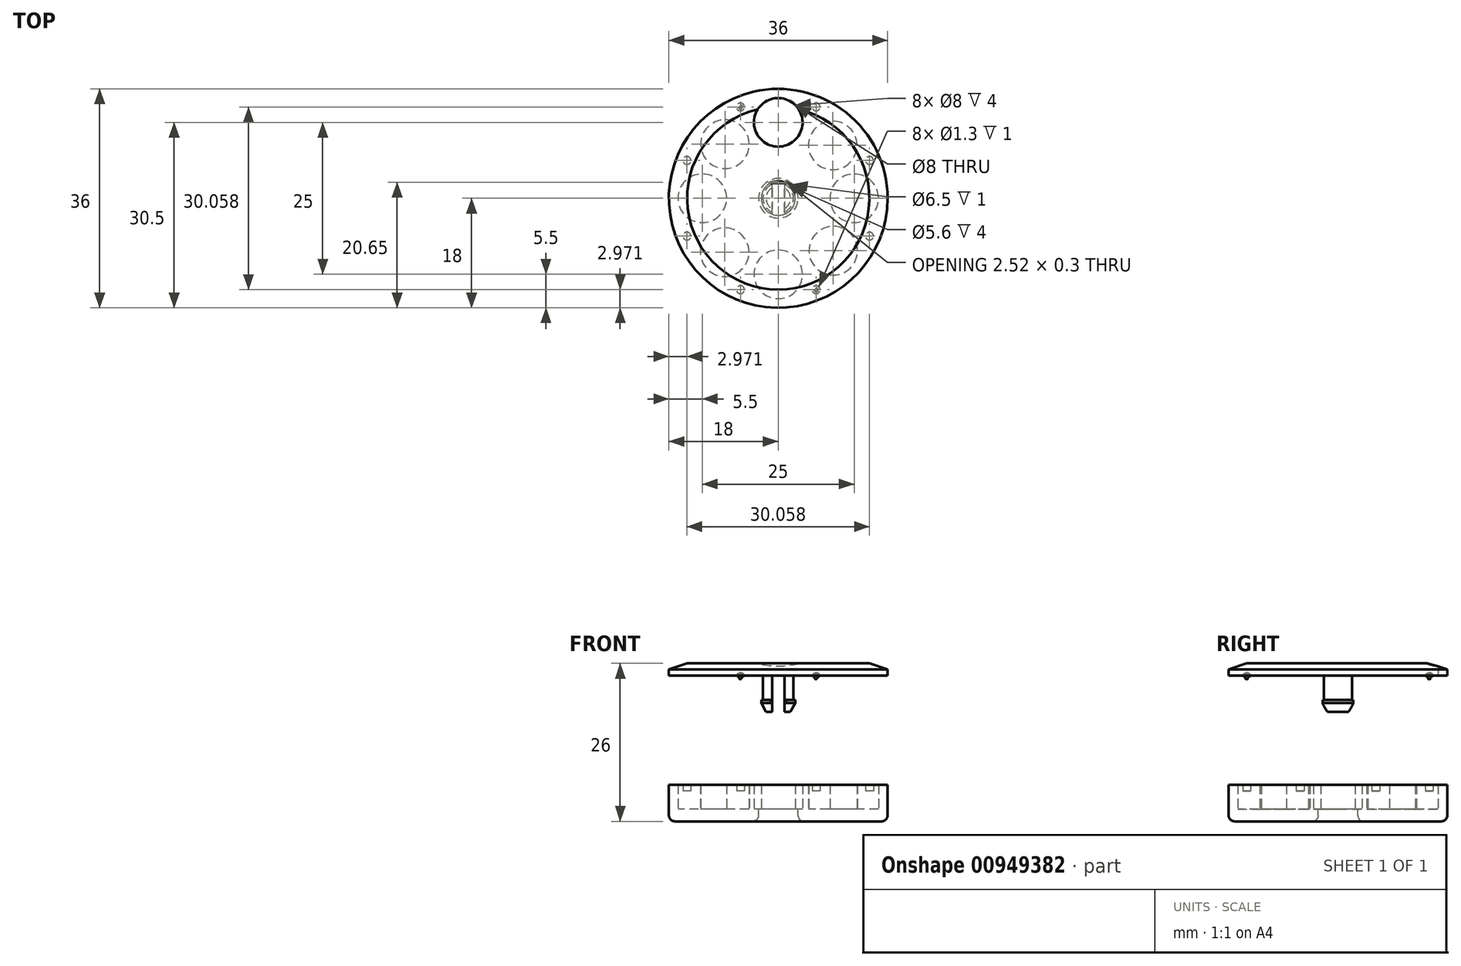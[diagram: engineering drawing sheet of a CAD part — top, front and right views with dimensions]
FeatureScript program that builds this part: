
annotation { "Feature Type Name" : "Feature", "Feature Type Description" : "" }
export const myFeature = defineFeature(function(context is Context, id is Id, definition is map)
    precondition{}
    {
        {
            var Q0;
            Q0=qCreatedBy(makeId("Top.planeOp"),FACE);
            var sketch = newSketch(context, id + "F0", { "sketchPlane" : qUnion([Q0])});
            skCircle(sketch, "E0", {"center": v(0, 0) * mm, "radius": 18 * mm});
            skCircle(sketch, "E1", {"center": v(0, 0) * mm, "radius": 12.5 * mm, "construction": true});
            skCircle(sketch, "E2", {"center": v(0, 12.5) * mm, "radius": 4 * mm});
            skCircle(sketch, "E3", {"center": v(12.5, 0) * mm, "radius": 4 * mm});
            skCircle(sketch, "E4", {"center": v(0, -12.5) * mm, "radius": 4 * mm});
            skCircle(sketch, "E5", {"center": v(-12.5, 0) * mm, "radius": 4 * mm});
            skCircle(sketch, "E6", {"center": v(8.97, 8.7) * mm, "radius": 4 * mm});
            skCircle(sketch, "E7", {"center": v(9.05, -8.62) * mm, "radius": 4 * mm});
            skCircle(sketch, "E8", {"center": v(-8.82, -8.86) * mm, "radius": 4 * mm});
            skCircle(sketch, "E9", {"center": v(-8.77, 8.9) * mm, "radius": 4 * mm});
            skCircle(sketch, "E10", {"center": v(0, 0) * mm, "radius": 2.5 * mm});
            skCircle(sketch, "E11", {"center": v(0, 0) * mm, "radius": 3.25 * mm});
            skLineSegment(sketch, "E12.bottom", {"start": v(1, 3.25) * mm, "end": v(-1, 3.25) * mm});
            skLineSegment(sketch, "E12.top", {"start": v(1, -3.25) * mm, "end": v(-1, -3.25) * mm});
            skLineSegment(sketch, "E12.left", {"start": v(1, 3.25) * mm, "end": v(1, -3.25) * mm});
            skLineSegment(sketch, "E12.right", {"start": v(-1, 3.25) * mm, "end": v(-1, -3.25) * mm});
            skLineSegment(sketch, "E13.bottom", {"start": v(3.25, 2.5) * mm, "end": v(-3.25, 2.5) * mm});
            skLineSegment(sketch, "E13.top", {"start": v(3.25, -2.5) * mm, "end": v(-3.25, -2.5) * mm});
            skLineSegment(sketch, "E13.left", {"start": v(3.25, 2.5) * mm, "end": v(3.25, -2.5) * mm});
            skLineSegment(sketch, "E13.right", {"start": v(-3.25, 2.5) * mm, "end": v(-3.25, -2.5) * mm});
            skCircle(sketch, "E14", {"center": v(0, 0) * mm, "radius": 2.8 * mm});
            skSolve(sketch);
        }
        {
            var Q0;
            Q0=makeQuery(id+"F0.imprint","IMPRINT",FACE,{"disambiguationData":[TD([[makeQuery(id+"F0.imprint","IMPRINT",EDGE,{"derivedFrom":sQuery(id+"F0.wireOp",EDGE,"E9")}),1.0]])]});
            var Q1;
            Q1=makeQuery(id+"F0.imprint","IMPRINT",FACE,{"disambiguationData":[TD([[makeQuery(id+"F0.imprint","IMPRINT",EDGE,{"derivedFrom":sQuery(id+"F0.wireOp",EDGE,"E2")}),1.0]])]});
            var Q2;
            Q2=makeQuery(id+"F0.imprint","IMPRINT",FACE,{"disambiguationData":[TD([[makeQuery(id+"F0.imprint","IMPRINT",EDGE,{"derivedFrom":sQuery(id+"F0.wireOp",EDGE,"E3")}),1.0]])]});
            var Q3;
            Q3=makeQuery(id+"F0.imprint","IMPRINT",FACE,{"disambiguationData":[TD([[makeQuery(id+"F0.imprint","IMPRINT",EDGE,{"derivedFrom":sQuery(id+"F0.wireOp",EDGE,"E7")}),1.0]])]});
            var Q4;
            Q4=makeQuery(id+"F0.imprint","IMPRINT",FACE,{"disambiguationData":[TD([[makeQuery(id+"F0.imprint","IMPRINT",EDGE,{"derivedFrom":sQuery(id+"F0.wireOp",EDGE,"E4")}),1.0]])]});
            var Q5;
            Q5=makeQuery(id+"F0.imprint","IMPRINT",FACE,{"disambiguationData":[TD([[makeQuery(id+"F0.imprint","IMPRINT",EDGE,{"derivedFrom":sQuery(id+"F0.wireOp",EDGE,"E6")}),1.0]])]});
            var Q6;
            Q6=makeQuery(id+"F0.imprint","IMPRINT",FACE,{"disambiguationData":[TD([[makeQuery(id+"F0.imprint","IMPRINT",EDGE,{"derivedFrom":sQuery(id+"F0.wireOp",EDGE,"E5")}),1.0]])]});
            var Q7;
            Q7=makeQuery(id+"F0.imprint","IMPRINT",FACE,{"disambiguationData":[TD([[makeQuery(id+"F0.imprint","IMPRINT",EDGE,{"derivedFrom":sQuery(id+"F0.wireOp",EDGE,"E8")}),1.0]])]});
            var Q8;
            Q8=makeQuery(id+"F0.imprint","IMPRINT",FACE,{"disambiguationData":[TD([[makeQuery(id+"F0.imprint","IMPRINT",EDGE,{"derivedFrom":sQuery(id+"F0.wireOp",EDGE,"E2")}),-1.0]])]});
            var Q9;
            {var subQ0=sQuery(id+"F0.wireOp",EDGE,"E12.bottom");var subQ1=sQuery(id+"F0.wireOp",EDGE,"E11");var subQ2=makeQuery(id+"F0.imprint","INTERSECT",VERTEX,{"derivedFrom":[subQ1,subQ0]});Q9=makeQuery(id+"F0.imprint","IMPRINT",FACE,{"disambiguationData":[TD([[makeQuery(id+"F0.imprint","IMPRINT",EDGE,{"disambiguationData":[TD([[subQ2,-1.0]])],"derivedFrom":subQ1}),-1.0]])]});}
            var Q10;
            {var subQ0=sQuery(id+"F0.wireOp",EDGE,"E12.bottom");var subQ1=sQuery(id+"F0.wireOp",EDGE,"E11");var subQ2=makeQuery(id+"F0.imprint","INTERSECT",VERTEX,{"derivedFrom":[subQ1,subQ0]});Q10=makeQuery(id+"F0.imprint","IMPRINT",FACE,{"disambiguationData":[TD([[makeQuery(id+"F0.imprint","IMPRINT",EDGE,{"disambiguationData":[TD([[subQ2,1.0]])],"derivedFrom":subQ1}),-1.0]])]});}
            var Q11;
            {var subQ0=sQuery(id+"F0.wireOp",EDGE,"E12.top");var subQ1=sQuery(id+"F0.wireOp",EDGE,"E11");var subQ2=makeQuery(id+"F0.imprint","INTERSECT",VERTEX,{"derivedFrom":[subQ1,subQ0]});Q11=makeQuery(id+"F0.imprint","IMPRINT",FACE,{"disambiguationData":[TD([[makeQuery(id+"F0.imprint","IMPRINT",EDGE,{"disambiguationData":[TD([[subQ2,-1.0]])],"derivedFrom":subQ1}),-1.0]])]});}
            var Q12;
            {var subQ0=sQuery(id+"F0.wireOp",EDGE,"E12.right");var subQ1=sQuery(id+"F0.wireOp",EDGE,"E11");var subQ2=makeQuery(id+"F0.imprint","INTERSECT",VERTEX,{"disambiguationData":[OD(1.0)],"derivedFrom":[subQ1,subQ0]});Q12=makeQuery(id+"F0.imprint","IMPRINT",FACE,{"disambiguationData":[TD([[makeQuery(id+"F0.imprint","IMPRINT",EDGE,{"disambiguationData":[TD([[subQ2,-1.0]])],"derivedFrom":subQ1}),-1.0]])]});}
            var Q13;
            {var subQ0=sQuery(id+"F0.wireOp",EDGE,"E13.bottom");var subQ1=sQuery(id+"F0.wireOp",EDGE,"E11");var subQ2=makeQuery(id+"F0.imprint","INTERSECT",VERTEX,{"disambiguationData":[OD(0.0)],"derivedFrom":[subQ1,subQ0]});Q13=makeQuery(id+"F0.imprint","IMPRINT",FACE,{"disambiguationData":[TD([[makeQuery(id+"F0.imprint","IMPRINT",EDGE,{"disambiguationData":[TD([[subQ2,1.0]])],"derivedFrom":subQ1}),-1.0]])]});}
            var Q14;
            {var subQ0=sQuery(id+"F0.wireOp",EDGE,"E13.left");var subQ1=sQuery(id+"F0.wireOp",EDGE,"E11");var subQ2=makeQuery(id+"F0.imprint","INTERSECT",VERTEX,{"derivedFrom":[subQ1,subQ0]});Q14=makeQuery(id+"F0.imprint","IMPRINT",FACE,{"disambiguationData":[TD([[makeQuery(id+"F0.imprint","IMPRINT",EDGE,{"disambiguationData":[TD([[subQ2,1.0]])],"derivedFrom":subQ1}),-1.0]])]});}
            var Q15;
            {var subQ0=sQuery(id+"F0.wireOp",EDGE,"E13.right");var subQ1=sQuery(id+"F0.wireOp",EDGE,"E11");var subQ2=makeQuery(id+"F0.imprint","INTERSECT",VERTEX,{"derivedFrom":[subQ1,subQ0]});Q15=makeQuery(id+"F0.imprint","IMPRINT",FACE,{"disambiguationData":[TD([[makeQuery(id+"F0.imprint","IMPRINT",EDGE,{"disambiguationData":[TD([[subQ2,-1.0]])],"derivedFrom":subQ1}),-1.0]])]});}
            var Q16;
            {var subQ0=sQuery(id+"F0.wireOp",EDGE,"E13.bottom");var subQ1=sQuery(id+"F0.wireOp",EDGE,"E11");var subQ2=makeQuery(id+"F0.imprint","INTERSECT",VERTEX,{"disambiguationData":[OD(1.0)],"derivedFrom":[subQ1,subQ0]});Q16=makeQuery(id+"F0.imprint","IMPRINT",FACE,{"disambiguationData":[TD([[makeQuery(id+"F0.imprint","IMPRINT",EDGE,{"disambiguationData":[TD([[subQ2,-1.0]])],"derivedFrom":subQ1}),-1.0]])]});}
            extrude(context, id + "F1", {"entities" : qUnion([Q0, Q1, Q2, Q3, Q4, Q5, Q6, Q7, Q8, Q9, Q10, Q11, Q12, Q13, Q14, Q15, Q16]), "oppositeDirection" : true, "depth" : 2 * mm, "offsetDistance" : 25 * mm});
        }
        {
            var Q0;
            Q0=makeQuery(id+"F0.imprint","IMPRINT",FACE,{"disambiguationData":[TD([[makeQuery(id+"F0.imprint","IMPRINT",EDGE,{"derivedFrom":sQuery(id+"F0.wireOp",EDGE,"E2")}),-1.0]])]});
            var Q1;
            {var subQ0=sQuery(id+"F0.wireOp",EDGE,"E13.bottom");var subQ1=sQuery(id+"F0.wireOp",EDGE,"E11");var subQ2=makeQuery(id+"F0.imprint","INTERSECT",VERTEX,{"disambiguationData":[OD(1.0)],"derivedFrom":[subQ1,subQ0]});Q1=makeQuery(id+"F0.imprint","IMPRINT",FACE,{"disambiguationData":[TD([[makeQuery(id+"F0.imprint","IMPRINT",EDGE,{"disambiguationData":[TD([[subQ2,-1.0]])],"derivedFrom":subQ1}),-1.0]])]});}
            var Q2;
            {var subQ1=sQuery(id+"F0.wireOp",EDGE,"E11");var subQ6=sQuery(id+"F0.wireOp",EDGE,"E12.left");var subQ7=makeQuery(id+"F0.imprint","INTERSECT",VERTEX,{"disambiguationData":[OD(0.0)],"derivedFrom":[subQ1,subQ6]});Q2=makeQuery(id+"F0.imprint","IMPRINT",FACE,{"disambiguationData":[TD([[makeQuery(id+"F0.imprint","IMPRINT",EDGE,{"disambiguationData":[TD([[subQ7,-1.0]])],"derivedFrom":subQ1}),1.0]])]});}
            var Q3;
            {var subQ0=sQuery(id+"F0.wireOp",EDGE,"E12.right");var subQ1=sQuery(id+"F0.wireOp",EDGE,"E11");var subQ2=makeQuery(id+"F0.imprint","INTERSECT",VERTEX,{"disambiguationData":[OD(0.0)],"derivedFrom":[subQ1,subQ0]});Q3=makeQuery(id+"F0.imprint","IMPRINT",FACE,{"disambiguationData":[TD([[makeQuery(id+"F0.imprint","IMPRINT",EDGE,{"disambiguationData":[TD([[subQ2,-1.0]])],"derivedFrom":subQ1}),1.0]])]});}
            var Q4;
            {var subQ0=sQuery(id+"F0.wireOp",EDGE,"E13.bottom");var subQ1=sQuery(id+"F0.wireOp",EDGE,"E11");var subQ2=makeQuery(id+"F0.imprint","INTERSECT",VERTEX,{"disambiguationData":[OD(0.0)],"derivedFrom":[subQ1,subQ0]});Q4=makeQuery(id+"F0.imprint","IMPRINT",FACE,{"disambiguationData":[TD([[makeQuery(id+"F0.imprint","IMPRINT",EDGE,{"disambiguationData":[TD([[subQ2,-1.0]])],"derivedFrom":subQ1}),1.0]])]});}
            var Q5;
            {var subQ1=sQuery(id+"F0.wireOp",EDGE,"E11");var subQ6=sQuery(id+"F0.wireOp",EDGE,"E13.bottom");var subQ7=makeQuery(id+"F0.imprint","INTERSECT",VERTEX,{"disambiguationData":[OD(0.0)],"derivedFrom":[subQ1,subQ6]});Q5=makeQuery(id+"F0.imprint","IMPRINT",FACE,{"disambiguationData":[TD([[makeQuery(id+"F0.imprint","IMPRINT",EDGE,{"disambiguationData":[TD([[subQ7,1.0]])],"derivedFrom":subQ1}),1.0]])]});}
            var Q6;
            {var subQ0=sQuery(id+"F0.wireOp",EDGE,"E12.left");var subQ1=sQuery(id+"F0.wireOp",EDGE,"E11");var subQ2=makeQuery(id+"F0.imprint","INTERSECT",VERTEX,{"disambiguationData":[OD(1.0)],"derivedFrom":[subQ1,subQ0]});Q6=makeQuery(id+"F0.imprint","IMPRINT",FACE,{"disambiguationData":[TD([[makeQuery(id+"F0.imprint","IMPRINT",EDGE,{"disambiguationData":[TD([[subQ2,-1.0]])],"derivedFrom":subQ1}),1.0]])]});}
            var Q7;
            {var subQ0=sQuery(id+"F0.wireOp",EDGE,"E13.left");var subQ1=sQuery(id+"F0.wireOp",EDGE,"E11");var subQ2=makeQuery(id+"F0.imprint","INTERSECT",VERTEX,{"derivedFrom":[subQ1,subQ0]});Q7=makeQuery(id+"F0.imprint","IMPRINT",FACE,{"disambiguationData":[TD([[makeQuery(id+"F0.imprint","IMPRINT",EDGE,{"disambiguationData":[TD([[subQ2,1.0]])],"derivedFrom":subQ1}),-1.0]])]});}
            var Q8;
            {var subQ0=sQuery(id+"F0.wireOp",EDGE,"E13.bottom");var subQ1=sQuery(id+"F0.wireOp",EDGE,"E11");var subQ2=makeQuery(id+"F0.imprint","INTERSECT",VERTEX,{"disambiguationData":[OD(0.0)],"derivedFrom":[subQ1,subQ0]});Q8=makeQuery(id+"F0.imprint","IMPRINT",FACE,{"disambiguationData":[TD([[makeQuery(id+"F0.imprint","IMPRINT",EDGE,{"disambiguationData":[TD([[subQ2,1.0]])],"derivedFrom":subQ1}),-1.0]])]});}
            var Q9;
            {var subQ0=sQuery(id+"F0.wireOp",EDGE,"E13.right");var subQ1=sQuery(id+"F0.wireOp",EDGE,"E11");var subQ2=makeQuery(id+"F0.imprint","INTERSECT",VERTEX,{"derivedFrom":[subQ1,subQ0]});Q9=makeQuery(id+"F0.imprint","IMPRINT",FACE,{"disambiguationData":[TD([[makeQuery(id+"F0.imprint","IMPRINT",EDGE,{"disambiguationData":[TD([[subQ2,-1.0]])],"derivedFrom":subQ1}),-1.0]])]});}
            var Q10;
            {var subQ0=sQuery(id+"F0.wireOp",EDGE,"E12.right");var subQ1=sQuery(id+"F0.wireOp",EDGE,"E11");var subQ2=makeQuery(id+"F0.imprint","INTERSECT",VERTEX,{"disambiguationData":[OD(1.0)],"derivedFrom":[subQ1,subQ0]});Q10=makeQuery(id+"F0.imprint","IMPRINT",FACE,{"disambiguationData":[TD([[makeQuery(id+"F0.imprint","IMPRINT",EDGE,{"disambiguationData":[TD([[subQ2,-1.0]])],"derivedFrom":subQ1}),1.0]])]});}
            var Q11;
            {var subQ0=sQuery(id+"F0.wireOp",EDGE,"E13.top");var subQ1=sQuery(id+"F0.wireOp",EDGE,"E11");var subQ2=makeQuery(id+"F0.imprint","INTERSECT",VERTEX,{"disambiguationData":[OD(0.0)],"derivedFrom":[subQ1,subQ0]});Q11=makeQuery(id+"F0.imprint","IMPRINT",FACE,{"disambiguationData":[TD([[makeQuery(id+"F0.imprint","IMPRINT",EDGE,{"disambiguationData":[TD([[subQ2,-1.0]])],"derivedFrom":subQ1}),1.0]])]});}
            var Q12;
            {var subQ1=sQuery(id+"F0.wireOp",EDGE,"E11");var subQ6=sQuery(id+"F0.wireOp",EDGE,"E13.bottom");var subQ7=makeQuery(id+"F0.imprint","INTERSECT",VERTEX,{"disambiguationData":[OD(1.0)],"derivedFrom":[subQ1,subQ6]});Q12=makeQuery(id+"F0.imprint","IMPRINT",FACE,{"disambiguationData":[TD([[makeQuery(id+"F0.imprint","IMPRINT",EDGE,{"disambiguationData":[TD([[subQ7,-1.0]])],"derivedFrom":subQ1}),1.0]])]});}
            var Q13;
            {var subQ0=sQuery(id+"F0.wireOp",EDGE,"E12.right");var subQ1=sQuery(id+"F0.wireOp",EDGE,"E11");var subQ2=makeQuery(id+"F0.imprint","INTERSECT",VERTEX,{"disambiguationData":[OD(1.0)],"derivedFrom":[subQ1,subQ0]});Q13=makeQuery(id+"F0.imprint","IMPRINT",FACE,{"disambiguationData":[TD([[makeQuery(id+"F0.imprint","IMPRINT",EDGE,{"disambiguationData":[TD([[subQ2,-1.0]])],"derivedFrom":subQ1}),-1.0]])]});}
            var Q14;
            {var subQ0=sQuery(id+"F0.wireOp",EDGE,"E12.top");var subQ1=sQuery(id+"F0.wireOp",EDGE,"E11");var subQ2=makeQuery(id+"F0.imprint","INTERSECT",VERTEX,{"derivedFrom":[subQ1,subQ0]});Q14=makeQuery(id+"F0.imprint","IMPRINT",FACE,{"disambiguationData":[TD([[makeQuery(id+"F0.imprint","IMPRINT",EDGE,{"disambiguationData":[TD([[subQ2,-1.0]])],"derivedFrom":subQ1}),-1.0]])]});}
            var Q15;
            {var subQ0=sQuery(id+"F0.wireOp",EDGE,"E12.bottom");var subQ1=sQuery(id+"F0.wireOp",EDGE,"E11");var subQ2=makeQuery(id+"F0.imprint","INTERSECT",VERTEX,{"derivedFrom":[subQ1,subQ0]});Q15=makeQuery(id+"F0.imprint","IMPRINT",FACE,{"disambiguationData":[TD([[makeQuery(id+"F0.imprint","IMPRINT",EDGE,{"disambiguationData":[TD([[subQ2,-1.0]])],"derivedFrom":subQ1}),-1.0]])]});}
            var Q16;
            {var subQ0=sQuery(id+"F0.wireOp",EDGE,"E12.left");var subQ1=sQuery(id+"F0.wireOp",EDGE,"E11");var subQ2=makeQuery(id+"F0.imprint","INTERSECT",VERTEX,{"disambiguationData":[OD(0.0)],"derivedFrom":[subQ1,subQ0]});Q16=makeQuery(id+"F0.imprint","IMPRINT",FACE,{"disambiguationData":[TD([[makeQuery(id+"F0.imprint","IMPRINT",EDGE,{"disambiguationData":[TD([[subQ2,-1.0]])],"derivedFrom":subQ1}),-1.0]])]});}
            extrude(context, id + "F2", {"entities" : qUnion([Q0, Q1, Q2, Q3, Q4, Q5, Q6, Q7, Q8, Q9, Q10, Q11, Q12, Q13, Q14, Q15, Q16]), "operationType" : NewBodyOperationType.ADD, "depth" : 4 * mm, "offsetDistance" : 25 * mm});
        }
        {
            var Q0;
            Q0=makeQuery(id+"F0.imprint","IMPRINT",FACE,{"disambiguationData":[TD([[makeQuery(id+"F0.imprint","IMPRINT",EDGE,{"derivedFrom":sQuery(id+"F0.wireOp",EDGE,"E2")}),-1.0]])]});
            var Q1;
            Q1=makeQuery(id+"F0.imprint","IMPRINT",FACE,{"disambiguationData":[TD([[makeQuery(id+"F0.imprint","IMPRINT",EDGE,{"derivedFrom":sQuery(id+"F0.wireOp",EDGE,"E8")}),1.0]])]});
            var Q2;
            Q2=makeQuery(id+"F0.imprint","IMPRINT",FACE,{"disambiguationData":[TD([[makeQuery(id+"F0.imprint","IMPRINT",EDGE,{"derivedFrom":sQuery(id+"F0.wireOp",EDGE,"E5")}),1.0]])]});
            var Q3;
            Q3=makeQuery(id+"F0.imprint","IMPRINT",FACE,{"disambiguationData":[TD([[makeQuery(id+"F0.imprint","IMPRINT",EDGE,{"derivedFrom":sQuery(id+"F0.wireOp",EDGE,"E9")}),1.0]])]});
            var Q4;
            Q4=makeQuery(id+"F0.imprint","IMPRINT",FACE,{"disambiguationData":[TD([[makeQuery(id+"F0.imprint","IMPRINT",EDGE,{"derivedFrom":sQuery(id+"F0.wireOp",EDGE,"E6")}),1.0]])]});
            var Q5;
            Q5=makeQuery(id+"F0.imprint","IMPRINT",FACE,{"disambiguationData":[TD([[makeQuery(id+"F0.imprint","IMPRINT",EDGE,{"derivedFrom":sQuery(id+"F0.wireOp",EDGE,"E3")}),1.0]])]});
            var Q6;
            Q6=makeQuery(id+"F0.imprint","IMPRINT",FACE,{"disambiguationData":[TD([[makeQuery(id+"F0.imprint","IMPRINT",EDGE,{"derivedFrom":sQuery(id+"F0.wireOp",EDGE,"E7")}),1.0]])]});
            var Q7;
            Q7=makeQuery(id+"F0.imprint","IMPRINT",FACE,{"disambiguationData":[TD([[makeQuery(id+"F0.imprint","IMPRINT",EDGE,{"derivedFrom":sQuery(id+"F0.wireOp",EDGE,"E4")}),1.0]])]});
            var Q8;
            {var subQ0=sQuery(id+"F0.wireOp",EDGE,"E13.bottom");var subQ1=sQuery(id+"F0.wireOp",EDGE,"E11");var subQ2=makeQuery(id+"F0.imprint","INTERSECT",VERTEX,{"disambiguationData":[OD(1.0)],"derivedFrom":[subQ1,subQ0]});Q8=makeQuery(id+"F0.imprint","IMPRINT",FACE,{"disambiguationData":[TD([[makeQuery(id+"F0.imprint","IMPRINT",EDGE,{"disambiguationData":[TD([[subQ2,-1.0]])],"derivedFrom":subQ1}),-1.0]])]});}
            var Q9;
            {var subQ0=sQuery(id+"F0.wireOp",EDGE,"E13.right");var subQ1=sQuery(id+"F0.wireOp",EDGE,"E11");var subQ2=makeQuery(id+"F0.imprint","INTERSECT",VERTEX,{"derivedFrom":[subQ1,subQ0]});Q9=makeQuery(id+"F0.imprint","IMPRINT",FACE,{"disambiguationData":[TD([[makeQuery(id+"F0.imprint","IMPRINT",EDGE,{"disambiguationData":[TD([[subQ2,-1.0]])],"derivedFrom":subQ1}),-1.0]])]});}
            var Q10;
            {var subQ0=sQuery(id+"F0.wireOp",EDGE,"E12.right");var subQ1=sQuery(id+"F0.wireOp",EDGE,"E11");var subQ2=makeQuery(id+"F0.imprint","INTERSECT",VERTEX,{"disambiguationData":[OD(1.0)],"derivedFrom":[subQ1,subQ0]});Q10=makeQuery(id+"F0.imprint","IMPRINT",FACE,{"disambiguationData":[TD([[makeQuery(id+"F0.imprint","IMPRINT",EDGE,{"disambiguationData":[TD([[subQ2,-1.0]])],"derivedFrom":subQ1}),-1.0]])]});}
            var Q11;
            {var subQ0=sQuery(id+"F0.wireOp",EDGE,"E12.top");var subQ1=sQuery(id+"F0.wireOp",EDGE,"E11");var subQ2=makeQuery(id+"F0.imprint","INTERSECT",VERTEX,{"derivedFrom":[subQ1,subQ0]});Q11=makeQuery(id+"F0.imprint","IMPRINT",FACE,{"disambiguationData":[TD([[makeQuery(id+"F0.imprint","IMPRINT",EDGE,{"disambiguationData":[TD([[subQ2,-1.0]])],"derivedFrom":subQ1}),-1.0]])]});}
            var Q12;
            {var subQ0=sQuery(id+"F0.wireOp",EDGE,"E13.left");var subQ1=sQuery(id+"F0.wireOp",EDGE,"E11");var subQ2=makeQuery(id+"F0.imprint","INTERSECT",VERTEX,{"derivedFrom":[subQ1,subQ0]});Q12=makeQuery(id+"F0.imprint","IMPRINT",FACE,{"disambiguationData":[TD([[makeQuery(id+"F0.imprint","IMPRINT",EDGE,{"disambiguationData":[TD([[subQ2,1.0]])],"derivedFrom":subQ1}),-1.0]])]});}
            var Q13;
            {var subQ0=sQuery(id+"F0.wireOp",EDGE,"E13.bottom");var subQ1=sQuery(id+"F0.wireOp",EDGE,"E11");var subQ2=makeQuery(id+"F0.imprint","INTERSECT",VERTEX,{"disambiguationData":[OD(0.0)],"derivedFrom":[subQ1,subQ0]});Q13=makeQuery(id+"F0.imprint","IMPRINT",FACE,{"disambiguationData":[TD([[makeQuery(id+"F0.imprint","IMPRINT",EDGE,{"disambiguationData":[TD([[subQ2,1.0]])],"derivedFrom":subQ1}),-1.0]])]});}
            var Q14;
            {var subQ0=sQuery(id+"F0.wireOp",EDGE,"E12.left");var subQ1=sQuery(id+"F0.wireOp",EDGE,"E11");var subQ2=makeQuery(id+"F0.imprint","INTERSECT",VERTEX,{"disambiguationData":[OD(0.0)],"derivedFrom":[subQ1,subQ0]});Q14=makeQuery(id+"F0.imprint","IMPRINT",FACE,{"disambiguationData":[TD([[makeQuery(id+"F0.imprint","IMPRINT",EDGE,{"disambiguationData":[TD([[subQ2,-1.0]])],"derivedFrom":subQ1}),-1.0]])]});}
            var Q15;
            {var subQ0=sQuery(id+"F0.wireOp",EDGE,"E12.bottom");var subQ1=sQuery(id+"F0.wireOp",EDGE,"E11");var subQ2=makeQuery(id+"F0.imprint","INTERSECT",VERTEX,{"derivedFrom":[subQ1,subQ0]});Q15=makeQuery(id+"F0.imprint","IMPRINT",FACE,{"disambiguationData":[TD([[makeQuery(id+"F0.imprint","IMPRINT",EDGE,{"disambiguationData":[TD([[subQ2,-1.0]])],"derivedFrom":subQ1}),-1.0]])]});}
            var Q16;
            {var subQ1=sQuery(id+"F0.wireOp",EDGE,"E11");var subQ6=sQuery(id+"F0.wireOp",EDGE,"E12.left");var subQ7=makeQuery(id+"F0.imprint","INTERSECT",VERTEX,{"disambiguationData":[OD(0.0)],"derivedFrom":[subQ1,subQ6]});Q16=makeQuery(id+"F0.imprint","IMPRINT",FACE,{"disambiguationData":[TD([[makeQuery(id+"F0.imprint","IMPRINT",EDGE,{"disambiguationData":[TD([[subQ7,-1.0]])],"derivedFrom":subQ1}),1.0]])]});}
            var Q17;
            {var subQ0=sQuery(id+"F0.wireOp",EDGE,"E12.right");var subQ1=sQuery(id+"F0.wireOp",EDGE,"E11");var subQ2=makeQuery(id+"F0.imprint","INTERSECT",VERTEX,{"disambiguationData":[OD(0.0)],"derivedFrom":[subQ1,subQ0]});Q17=makeQuery(id+"F0.imprint","IMPRINT",FACE,{"disambiguationData":[TD([[makeQuery(id+"F0.imprint","IMPRINT",EDGE,{"disambiguationData":[TD([[subQ2,-1.0]])],"derivedFrom":subQ1}),1.0]])]});}
            var Q18;
            {var subQ1=sQuery(id+"F0.wireOp",EDGE,"E11");var subQ6=sQuery(id+"F0.wireOp",EDGE,"E13.bottom");var subQ7=makeQuery(id+"F0.imprint","INTERSECT",VERTEX,{"disambiguationData":[OD(0.0)],"derivedFrom":[subQ1,subQ6]});Q18=makeQuery(id+"F0.imprint","IMPRINT",FACE,{"disambiguationData":[TD([[makeQuery(id+"F0.imprint","IMPRINT",EDGE,{"disambiguationData":[TD([[subQ7,1.0]])],"derivedFrom":subQ1}),1.0]])]});}
            var Q19;
            {var subQ0=sQuery(id+"F0.wireOp",EDGE,"E12.left");var subQ1=sQuery(id+"F0.wireOp",EDGE,"E11");var subQ2=makeQuery(id+"F0.imprint","INTERSECT",VERTEX,{"disambiguationData":[OD(1.0)],"derivedFrom":[subQ1,subQ0]});Q19=makeQuery(id+"F0.imprint","IMPRINT",FACE,{"disambiguationData":[TD([[makeQuery(id+"F0.imprint","IMPRINT",EDGE,{"disambiguationData":[TD([[subQ2,-1.0]])],"derivedFrom":subQ1}),1.0]])]});}
            var Q20;
            {var subQ0=sQuery(id+"F0.wireOp",EDGE,"E12.right");var subQ1=sQuery(id+"F0.wireOp",EDGE,"E11");var subQ2=makeQuery(id+"F0.imprint","INTERSECT",VERTEX,{"disambiguationData":[OD(1.0)],"derivedFrom":[subQ1,subQ0]});Q20=makeQuery(id+"F0.imprint","IMPRINT",FACE,{"disambiguationData":[TD([[makeQuery(id+"F0.imprint","IMPRINT",EDGE,{"disambiguationData":[TD([[subQ2,-1.0]])],"derivedFrom":subQ1}),1.0]])]});}
            var Q21;
            {var subQ0=sQuery(id+"F0.wireOp",EDGE,"E13.top");var subQ1=sQuery(id+"F0.wireOp",EDGE,"E11");var subQ2=makeQuery(id+"F0.imprint","INTERSECT",VERTEX,{"disambiguationData":[OD(0.0)],"derivedFrom":[subQ1,subQ0]});Q21=makeQuery(id+"F0.imprint","IMPRINT",FACE,{"disambiguationData":[TD([[makeQuery(id+"F0.imprint","IMPRINT",EDGE,{"disambiguationData":[TD([[subQ2,-1.0]])],"derivedFrom":subQ1}),1.0]])]});}
            var Q22;
            {var subQ1=sQuery(id+"F0.wireOp",EDGE,"E11");var subQ6=sQuery(id+"F0.wireOp",EDGE,"E13.bottom");var subQ7=makeQuery(id+"F0.imprint","INTERSECT",VERTEX,{"disambiguationData":[OD(1.0)],"derivedFrom":[subQ1,subQ6]});Q22=makeQuery(id+"F0.imprint","IMPRINT",FACE,{"disambiguationData":[TD([[makeQuery(id+"F0.imprint","IMPRINT",EDGE,{"disambiguationData":[TD([[subQ7,-1.0]])],"derivedFrom":subQ1}),1.0]])]});}
            var Q23;
            {var subQ0=sQuery(id+"F0.wireOp",EDGE,"E13.top");var subQ1=sQuery(id+"F0.wireOp",EDGE,"E12.right");var subQ2=makeQuery(id+"F0.imprint","INTERSECT",VERTEX,{"derivedFrom":[subQ1,subQ0]});Q23=makeQuery(id+"F0.imprint","IMPRINT",FACE,{"disambiguationData":[TD([[makeQuery(id+"F0.imprint","IMPRINT",EDGE,{"disambiguationData":[TD([[subQ2,-1.0]])],"derivedFrom":subQ1}),-1.0]])]});}
            var Q24;
            {var subQ0=sQuery(id+"F0.wireOp",EDGE,"E13.top");var subQ2=sQuery(id+"F0.wireOp",EDGE,"E12.left");var subQ3=makeQuery(id+"F0.imprint","INTERSECT",VERTEX,{"derivedFrom":[subQ2,subQ0]});Q24=makeQuery(id+"F0.imprint","IMPRINT",FACE,{"disambiguationData":[TD([[makeQuery(id+"F0.imprint","IMPRINT",EDGE,{"disambiguationData":[TD([[subQ3,-1.0]])],"derivedFrom":subQ2}),-1.0]])]});}
            var Q25;
            {var subQ0=sQuery(id+"F0.wireOp",EDGE,"E13.top");var subQ1=sQuery(id+"F0.wireOp",EDGE,"E12.left");var subQ2=makeQuery(id+"F0.imprint","INTERSECT",VERTEX,{"derivedFrom":[subQ1,subQ0]});Q25=makeQuery(id+"F0.imprint","IMPRINT",FACE,{"disambiguationData":[TD([[makeQuery(id+"F0.imprint","IMPRINT",EDGE,{"disambiguationData":[TD([[subQ2,-1.0]])],"derivedFrom":subQ1}),1.0]])]});}
            var Q26;
            {var subQ1=sQuery(id+"F0.wireOp",EDGE,"E12.left");var subQ5=sQuery(id+"F0.wireOp",EDGE,"E10");var subQ9=makeQuery(id+"F0.imprint","INTERSECT",VERTEX,{"disambiguationData":[OD(0.0)],"derivedFrom":[subQ5,subQ1]});Q26=makeQuery(id+"F0.imprint","IMPRINT",FACE,{"disambiguationData":[TD([[makeQuery(id+"F0.imprint","IMPRINT",EDGE,{"disambiguationData":[TD([[subQ9,1.0]])],"derivedFrom":subQ5}),-1.0]])]});}
            var Q27;
            {var subQ0=sQuery(id+"F0.wireOp",EDGE,"E13.top");var subQ1=sQuery(id+"F0.wireOp",EDGE,"E10");var subQ2=makeQuery(id+"F0.imprint","INTERSECT",VERTEX,{"derivedFrom":[subQ1,subQ0]});Q27=makeQuery(id+"F0.imprint","IMPRINT",FACE,{"disambiguationData":[TD([[makeQuery(id+"F0.imprint","IMPRINT",EDGE,{"disambiguationData":[TD([[subQ2,-1.0]])],"derivedFrom":subQ1}),-1.0]])]});}
            var Q28;
            {var subQ0=sQuery(id+"F0.wireOp",EDGE,"E12.right");var subQ1=sQuery(id+"F0.wireOp",EDGE,"E10");var subQ2=makeQuery(id+"F0.imprint","INTERSECT",VERTEX,{"disambiguationData":[OD(1.0)],"derivedFrom":[subQ1,subQ0]});Q28=makeQuery(id+"F0.imprint","IMPRINT",FACE,{"disambiguationData":[TD([[makeQuery(id+"F0.imprint","IMPRINT",EDGE,{"disambiguationData":[TD([[subQ2,-1.0]])],"derivedFrom":subQ1}),-1.0]])]});}
            var Q29;
            {var subQ1=sQuery(id+"F0.wireOp",EDGE,"E12.right");var subQ5=sQuery(id+"F0.wireOp",EDGE,"E10");var subQ6=makeQuery(id+"F0.imprint","INTERSECT",VERTEX,{"disambiguationData":[OD(0.0)],"derivedFrom":[subQ5,subQ1]});Q29=makeQuery(id+"F0.imprint","IMPRINT",FACE,{"disambiguationData":[TD([[makeQuery(id+"F0.imprint","IMPRINT",EDGE,{"disambiguationData":[TD([[subQ6,-1.0]])],"derivedFrom":subQ5}),-1.0]])]});}
            var Q30;
            {var subQ0=sQuery(id+"F0.wireOp",EDGE,"E13.bottom");var subQ1=sQuery(id+"F0.wireOp",EDGE,"E10");var subQ2=makeQuery(id+"F0.imprint","INTERSECT",VERTEX,{"derivedFrom":[subQ1,subQ0]});Q30=makeQuery(id+"F0.imprint","IMPRINT",FACE,{"disambiguationData":[TD([[makeQuery(id+"F0.imprint","IMPRINT",EDGE,{"disambiguationData":[TD([[subQ2,-1.0]])],"derivedFrom":subQ1}),-1.0]])]});}
            var Q31;
            {var subQ0=sQuery(id+"F0.wireOp",EDGE,"E14");var subQ1=sQuery(id+"F0.wireOp",EDGE,"E12.right");var subQ2=makeQuery(id+"F0.imprint","INTERSECT",VERTEX,{"disambiguationData":[OD(0.0)],"derivedFrom":[subQ1,subQ0]});Q31=makeQuery(id+"F0.imprint","IMPRINT",FACE,{"disambiguationData":[TD([[makeQuery(id+"F0.imprint","IMPRINT",EDGE,{"disambiguationData":[TD([[subQ2,-1.0]])],"derivedFrom":subQ1}),-1.0]])]});}
            var Q32;
            {var subQ0=sQuery(id+"F0.wireOp",EDGE,"E13.bottom");var subQ1=sQuery(id+"F0.wireOp",EDGE,"E11");var subQ2=makeQuery(id+"F0.imprint","INTERSECT",VERTEX,{"disambiguationData":[OD(0.0)],"derivedFrom":[subQ1,subQ0]});Q32=makeQuery(id+"F0.imprint","IMPRINT",FACE,{"disambiguationData":[TD([[makeQuery(id+"F0.imprint","IMPRINT",EDGE,{"disambiguationData":[TD([[subQ2,-1.0]])],"derivedFrom":subQ1}),1.0]])]});}
            var Q33;
            {var subQ0=sQuery(id+"F0.wireOp",EDGE,"E14");var subQ1=sQuery(id+"F0.wireOp",EDGE,"E12.left");var subQ2=makeQuery(id+"F0.imprint","INTERSECT",VERTEX,{"disambiguationData":[OD(0.0)],"derivedFrom":[subQ1,subQ0]});Q33=makeQuery(id+"F0.imprint","IMPRINT",FACE,{"disambiguationData":[TD([[makeQuery(id+"F0.imprint","IMPRINT",EDGE,{"disambiguationData":[TD([[subQ2,-1.0]])],"derivedFrom":subQ1}),1.0]])]});}
            var Q34;
            {var subQ2=sQuery(id+"F0.wireOp",EDGE,"E12.left");var subQ4=sQuery(id+"F0.wireOp",EDGE,"E14");var subQ8=makeQuery(id+"F0.imprint","INTERSECT",VERTEX,{"disambiguationData":[OD(0.0)],"derivedFrom":[subQ2,subQ4]});Q34=makeQuery(id+"F0.imprint","IMPRINT",FACE,{"disambiguationData":[TD([[makeQuery(id+"F0.imprint","IMPRINT",EDGE,{"disambiguationData":[TD([[subQ8,-1.0]])],"derivedFrom":subQ2}),-1.0]])]});}
            var Q35;
            {var subQ0=sQuery(id+"F0.wireOp",EDGE,"E13.bottom");var subQ1=sQuery(id+"F0.wireOp",EDGE,"E10");var subQ2=makeQuery(id+"F0.imprint","INTERSECT",VERTEX,{"derivedFrom":[subQ1,subQ0]});Q35=makeQuery(id+"F0.imprint","IMPRINT",FACE,{"disambiguationData":[TD([[makeQuery(id+"F0.imprint","IMPRINT",EDGE,{"disambiguationData":[TD([[subQ2,1.0]])],"derivedFrom":subQ1}),-1.0]])]});}
            var Q36;
            {var subQ0=sQuery(id+"F0.wireOp",EDGE,"E12.left");var subQ1=sQuery(id+"F0.wireOp",EDGE,"E10");var subQ2=makeQuery(id+"F0.imprint","INTERSECT",VERTEX,{"disambiguationData":[OD(0.0)],"derivedFrom":[subQ1,subQ0]});Q36=makeQuery(id+"F0.imprint","IMPRINT",FACE,{"disambiguationData":[TD([[makeQuery(id+"F0.imprint","IMPRINT",EDGE,{"disambiguationData":[TD([[subQ2,1.0]])],"derivedFrom":subQ1}),1.0]])]});}
            var Q37;
            {var subQ0=sQuery(id+"F0.wireOp",EDGE,"E10");var subQ7=makeQuery(id+"F0.imprint","INTERSECT",VERTEX,{"derivedFrom":[subQ0,sQuery(id+"F0.wireOp",EDGE,"E13.bottom")]});Q37=makeQuery(id+"F0.imprint","IMPRINT",FACE,{"disambiguationData":[TD([[makeQuery(id+"F0.imprint","IMPRINT",EDGE,{"disambiguationData":[TD([[subQ7,1.0]])],"derivedFrom":subQ0}),1.0]])]});}
            var Q38;
            {var subQ0=sQuery(id+"F0.wireOp",EDGE,"E12.right");var subQ1=sQuery(id+"F0.wireOp",EDGE,"E10");var subQ2=makeQuery(id+"F0.imprint","INTERSECT",VERTEX,{"disambiguationData":[OD(0.0)],"derivedFrom":[subQ1,subQ0]});Q38=makeQuery(id+"F0.imprint","IMPRINT",FACE,{"disambiguationData":[TD([[makeQuery(id+"F0.imprint","IMPRINT",EDGE,{"disambiguationData":[TD([[subQ2,-1.0]])],"derivedFrom":subQ1}),1.0]])]});}
            extrude(context, id + "F3", {"entities" : qUnion([Q0, Q1, Q2, Q3, Q4, Q5, Q6, Q7, Q8, Q9, Q10, Q11, Q12, Q13, Q14, Q15, Q16, Q17, Q18, Q19, Q20, Q21, Q22, Q23, Q24, Q25, Q26, Q27, Q28, Q29, Q30, Q31, Q32, Q33, Q34, Q35, Q36, Q37, Q38]), "depth" : 24 * mm, "offsetDistance" : 25 * mm, "hasSecondDirection" : true, "secondDirectionOppositeDirection" : false, "secondDirectionDepth" : 22 * mm});
        }
        {
            var Q0;
            {var subQ0=sQuery(id+"F0.wireOp",EDGE,"E12.left");var subQ1=sQuery(id+"F0.wireOp",EDGE,"E10");var subQ2=makeQuery(id+"F0.imprint","INTERSECT",VERTEX,{"disambiguationData":[OD(0.0)],"derivedFrom":[subQ1,subQ0]});Q0=makeQuery(id+"F0.imprint","IMPRINT",FACE,{"disambiguationData":[TD([[makeQuery(id+"F0.imprint","IMPRINT",EDGE,{"disambiguationData":[TD([[subQ2,1.0]])],"derivedFrom":subQ1}),1.0]])]});}
            var Q1;
            {var subQ0=sQuery(id+"F0.wireOp",EDGE,"E12.right");var subQ1=sQuery(id+"F0.wireOp",EDGE,"E10");var subQ2=makeQuery(id+"F0.imprint","INTERSECT",VERTEX,{"disambiguationData":[OD(0.0)],"derivedFrom":[subQ1,subQ0]});Q1=makeQuery(id+"F0.imprint","IMPRINT",FACE,{"disambiguationData":[TD([[makeQuery(id+"F0.imprint","IMPRINT",EDGE,{"disambiguationData":[TD([[subQ2,-1.0]])],"derivedFrom":subQ1}),1.0]])]});}
            extrude(context, id + "F4", {"entities" : qUnion([Q0, Q1]), "operationType" : NewBodyOperationType.ADD, "depth" : 24 * mm, "offsetDistance" : 25 * mm, "hasSecondDirection" : true, "secondDirectionOppositeDirection" : false, "secondDirectionDepth" : 16 * mm});
        }
        {
            var Q0;
            {var subQ0=sQuery(id+"F0.wireOp",EDGE,"E12.left");var subQ1=sQuery(id+"F0.wireOp",EDGE,"E10");var subQ2=makeQuery(id+"F0.imprint","INTERSECT",VERTEX,{"disambiguationData":[OD(0.0)],"derivedFrom":[subQ1,subQ0]});Q0=makeQuery(id+"F0.imprint","IMPRINT",FACE,{"disambiguationData":[TD([[makeQuery(id+"F0.imprint","IMPRINT",EDGE,{"disambiguationData":[TD([[subQ2,1.0]])],"derivedFrom":subQ1}),-1.0]])]});}
            var Q1;
            {var subQ0=sQuery(id+"F0.wireOp",EDGE,"E12.right");var subQ1=sQuery(id+"F0.wireOp",EDGE,"E10");var subQ2=makeQuery(id+"F0.imprint","INTERSECT",VERTEX,{"disambiguationData":[OD(0.0)],"derivedFrom":[subQ1,subQ0]});Q1=makeQuery(id+"F0.imprint","IMPRINT",FACE,{"disambiguationData":[TD([[makeQuery(id+"F0.imprint","IMPRINT",EDGE,{"disambiguationData":[TD([[subQ2,-1.0]])],"derivedFrom":subQ1}),-1.0]])]});}
            extrude(context, id + "F5", {"entities" : qUnion([Q0, Q1]), "operationType" : NewBodyOperationType.ADD, "depth" : 18 * mm, "offsetDistance" : 25 * mm, "hasSecondDirection" : true, "secondDirectionOppositeDirection" : false, "secondDirectionDepth" : 16 * mm});
        }
        {
            var Q0;
            Q0=makeQuery(id+"F3.opExtrude","CAP_EDGE",EDGE,{"disambiguationData":[OSD([sQuery(id+"F0.wireOp",EDGE,"E0")])],"isStart":false});
            chamfer(context, id + "F6", {"entities" : qUnion([Q0]), "chamferType" : ChamferType.TWO_OFFSETS, "width1" : 3 * mm, "oppositeDirection" : false, "width2" : 1 * mm, "tangentPropagation" : true});
        }
        {
            var Q0;
            {var subQ0=sQuery(id+"F0.wireOp",EDGE,"E14");Q0=makeQuery(id+"F5.opExtrude","CAP_EDGE",EDGE,{"disambiguationData":[OSD([subQ0]),TDD([makeQuery(id+"F0.imprint","IMPRINT",EDGE,{"disambiguationData":[TD([[makeQuery(id+"F0.imprint","INTERSECT",VERTEX,{"disambiguationData":[OD(1.0)],"derivedFrom":[sQuery(id+"F0.wireOp",EDGE,"E13.bottom"),subQ0]}),-1.0]])],"derivedFrom":subQ0})])],"isStart":true});}
            var Q1;
            {var subQ0=sQuery(id+"F0.wireOp",EDGE,"E14");Q1=makeQuery(id+"F5.opExtrude","CAP_EDGE",EDGE,{"disambiguationData":[OSD([subQ0]),TDD([makeQuery(id+"F0.imprint","IMPRINT",EDGE,{"disambiguationData":[TD([[makeQuery(id+"F0.imprint","INTERSECT",VERTEX,{"disambiguationData":[OD(0.0)],"derivedFrom":[sQuery(id+"F0.wireOp",EDGE,"E13.bottom"),subQ0]}),1.0]])],"derivedFrom":subQ0})])],"isStart":true});}
            chamfer(context, id + "F7", {"entities" : qUnion([Q0, Q1]), "chamferType" : ChamferType.TWO_OFFSETS, "width1" : 1.5 * mm, "oppositeDirection" : false, "width2" : 0.8 * mm, "tangentPropagation" : true});
        }
        {
            var Q0;
            Q0=makeQuery(id+"F1.opExtrude","CAP_EDGE",EDGE,{"disambiguationData":[OSD([sQuery(id+"F0.wireOp",EDGE,"E0")])],"isStart":false});
            var Q1;
            Q1=makeQuery(id+"F1.opExtrude","CAP_EDGE",EDGE,{"disambiguationData":[OSD([sQuery(id+"F0.wireOp",EDGE,"E11")])],"isStart":false});
            fillet(context, id + "F8", {"entities" : qUnion([Q0, Q1]), "radius" : 1 * mm, "tangentPropagation" : true, "allowEdgeOverflow" : false});
        }
        {
            var Q0;
            Q0=qCreatedBy(makeId("Top.planeOp"),FACE);
            var sketch = newSketch(context, id + "F9", { "sketchPlane" : qUnion([Q0])});
            skCircle(sketch, "E15.cCircle", {"center": v(0, 0) * mm, "radius": 15.03 * mm, "construction": true});
            skLineSegment(sketch, "E15.0", {"start": v(-6.23, 15.03) * mm, "end": v(6.23, 15.03) * mm});
            skLineSegment(sketch, "E15.1", {"start": v(6.23, 15.03) * mm, "end": v(15.03, 6.23) * mm});
            skLineSegment(sketch, "E15.2", {"start": v(15.03, 6.23) * mm, "end": v(15.03, -6.23) * mm});
            skLineSegment(sketch, "E15.3", {"start": v(15.03, -6.23) * mm, "end": v(6.23, -15.03) * mm});
            skLineSegment(sketch, "E15.4", {"start": v(6.23, -15.03) * mm, "end": v(-6.23, -15.03) * mm});
            skLineSegment(sketch, "E15.5", {"start": v(-6.23, -15.03) * mm, "end": v(-15.03, -6.23) * mm});
            skLineSegment(sketch, "E15.6", {"start": v(-15.03, -6.23) * mm, "end": v(-15.03, 6.23) * mm});
            skLineSegment(sketch, "E15.7", {"start": v(-15.03, 6.23) * mm, "end": v(-6.23, 15.03) * mm});
            skPoint(sketch, "E15.0.midPoint", {"position": v(0, 15.03) * mm});
            skCircle(sketch, "E16", {"center": v(-6.23, 15.03) * mm, "radius": 0.65 * mm});
            skCircle(sketch, "E17", {"center": v(6.23, 15.03) * mm, "radius": 0.65 * mm});
            skCircle(sketch, "E18", {"center": v(15.03, 6.23) * mm, "radius": 0.65 * mm});
            skCircle(sketch, "E19", {"center": v(15.03, -6.23) * mm, "radius": 0.65 * mm});
            skCircle(sketch, "E20", {"center": v(6.23, -15.03) * mm, "radius": 0.65 * mm});
            skCircle(sketch, "E21", {"center": v(-6.23, -15.03) * mm, "radius": 0.65 * mm});
            skCircle(sketch, "E22", {"center": v(-15.03, -6.23) * mm, "radius": 0.65 * mm});
            skCircle(sketch, "E23", {"center": v(-15.03, 6.23) * mm, "radius": 0.65 * mm});
            skSolve(sketch);
        }
        {
            var Q0;
            {var subQ0=sQuery(id+"F9.wireOp",EDGE,"E15.7");var subQ1=sQuery(id+"F9.wireOp",EDGE,"E15.0");var subQ2=makeQuery(id+"F9.imprint","INTERSECT",VERTEX,{"derivedFrom":[subQ1,subQ0]});Q0=makeQuery(id+"F9.imprint","IMPRINT",FACE,{"disambiguationData":[TD([[makeQuery(id+"F9.imprint","IMPRINT",EDGE,{"disambiguationData":[TD([[subQ2,-1.0]])],"derivedFrom":subQ1}),1.0]])]});}
            var Q1;
            {var subQ0=sQuery(id+"F9.wireOp",EDGE,"E15.7");var subQ1=sQuery(id+"F9.wireOp",EDGE,"E15.0");var subQ2=makeQuery(id+"F9.imprint","INTERSECT",VERTEX,{"derivedFrom":[subQ1,subQ0]});Q1=makeQuery(id+"F9.imprint","IMPRINT",FACE,{"disambiguationData":[TD([[makeQuery(id+"F9.imprint","IMPRINT",EDGE,{"disambiguationData":[TD([[subQ2,-1.0]])],"derivedFrom":subQ1}),-1.0]])]});}
            var Q2;
            {var subQ0=sQuery(id+"F9.wireOp",EDGE,"E15.7");var subQ1=sQuery(id+"F9.wireOp",EDGE,"E15.6");var subQ2=makeQuery(id+"F9.imprint","INTERSECT",VERTEX,{"derivedFrom":[subQ1,subQ0]});Q2=makeQuery(id+"F9.imprint","IMPRINT",FACE,{"disambiguationData":[TD([[makeQuery(id+"F9.imprint","IMPRINT",EDGE,{"disambiguationData":[TD([[subQ2,1.0]])],"derivedFrom":subQ1}),-1.0]])]});}
            var Q3;
            {var subQ0=sQuery(id+"F9.wireOp",EDGE,"E15.7");var subQ1=sQuery(id+"F9.wireOp",EDGE,"E15.6");var subQ2=makeQuery(id+"F9.imprint","INTERSECT",VERTEX,{"derivedFrom":[subQ1,subQ0]});Q3=makeQuery(id+"F9.imprint","IMPRINT",FACE,{"disambiguationData":[TD([[makeQuery(id+"F9.imprint","IMPRINT",EDGE,{"disambiguationData":[TD([[subQ2,1.0]])],"derivedFrom":subQ1}),1.0]])]});}
            var Q4;
            {var subQ0=sQuery(id+"F9.wireOp",EDGE,"E15.1");var subQ1=sQuery(id+"F9.wireOp",EDGE,"E15.0");var subQ2=makeQuery(id+"F9.imprint","INTERSECT",VERTEX,{"derivedFrom":[subQ1,subQ0]});Q4=makeQuery(id+"F9.imprint","IMPRINT",FACE,{"disambiguationData":[TD([[makeQuery(id+"F9.imprint","IMPRINT",EDGE,{"disambiguationData":[TD([[subQ2,1.0]])],"derivedFrom":subQ1}),-1.0]])]});}
            var Q5;
            {var subQ0=sQuery(id+"F9.wireOp",EDGE,"E15.1");var subQ1=sQuery(id+"F9.wireOp",EDGE,"E15.0");var subQ2=makeQuery(id+"F9.imprint","INTERSECT",VERTEX,{"derivedFrom":[subQ1,subQ0]});Q5=makeQuery(id+"F9.imprint","IMPRINT",FACE,{"disambiguationData":[TD([[makeQuery(id+"F9.imprint","IMPRINT",EDGE,{"disambiguationData":[TD([[subQ2,1.0]])],"derivedFrom":subQ1}),1.0]])]});}
            var Q6;
            {var subQ0=sQuery(id+"F9.wireOp",EDGE,"E15.2");var subQ1=sQuery(id+"F9.wireOp",EDGE,"E15.1");var subQ2=makeQuery(id+"F9.imprint","INTERSECT",VERTEX,{"derivedFrom":[subQ1,subQ0]});Q6=makeQuery(id+"F9.imprint","IMPRINT",FACE,{"disambiguationData":[TD([[makeQuery(id+"F9.imprint","IMPRINT",EDGE,{"disambiguationData":[TD([[subQ2,1.0]])],"derivedFrom":subQ1}),-1.0]])]});}
            var Q7;
            {var subQ0=sQuery(id+"F9.wireOp",EDGE,"E15.2");var subQ1=sQuery(id+"F9.wireOp",EDGE,"E15.1");var subQ2=makeQuery(id+"F9.imprint","INTERSECT",VERTEX,{"derivedFrom":[subQ1,subQ0]});Q7=makeQuery(id+"F9.imprint","IMPRINT",FACE,{"disambiguationData":[TD([[makeQuery(id+"F9.imprint","IMPRINT",EDGE,{"disambiguationData":[TD([[subQ2,1.0]])],"derivedFrom":subQ1}),1.0]])]});}
            var Q8;
            {var subQ0=sQuery(id+"F9.wireOp",EDGE,"E15.3");var subQ1=sQuery(id+"F9.wireOp",EDGE,"E15.2");var subQ2=makeQuery(id+"F9.imprint","INTERSECT",VERTEX,{"derivedFrom":[subQ1,subQ0]});Q8=makeQuery(id+"F9.imprint","IMPRINT",FACE,{"disambiguationData":[TD([[makeQuery(id+"F9.imprint","IMPRINT",EDGE,{"disambiguationData":[TD([[subQ2,1.0]])],"derivedFrom":subQ1}),1.0]])]});}
            var Q9;
            {var subQ0=sQuery(id+"F9.wireOp",EDGE,"E15.3");var subQ1=sQuery(id+"F9.wireOp",EDGE,"E15.2");var subQ2=makeQuery(id+"F9.imprint","INTERSECT",VERTEX,{"derivedFrom":[subQ1,subQ0]});Q9=makeQuery(id+"F9.imprint","IMPRINT",FACE,{"disambiguationData":[TD([[makeQuery(id+"F9.imprint","IMPRINT",EDGE,{"disambiguationData":[TD([[subQ2,1.0]])],"derivedFrom":subQ1}),-1.0]])]});}
            var Q10;
            {var subQ0=sQuery(id+"F9.wireOp",EDGE,"E15.4");var subQ1=sQuery(id+"F9.wireOp",EDGE,"E15.3");var subQ2=makeQuery(id+"F9.imprint","INTERSECT",VERTEX,{"derivedFrom":[subQ1,subQ0]});Q10=makeQuery(id+"F9.imprint","IMPRINT",FACE,{"disambiguationData":[TD([[makeQuery(id+"F9.imprint","IMPRINT",EDGE,{"disambiguationData":[TD([[subQ2,1.0]])],"derivedFrom":subQ1}),1.0]])]});}
            var Q11;
            {var subQ0=sQuery(id+"F9.wireOp",EDGE,"E15.4");var subQ1=sQuery(id+"F9.wireOp",EDGE,"E15.3");var subQ2=makeQuery(id+"F9.imprint","INTERSECT",VERTEX,{"derivedFrom":[subQ1,subQ0]});Q11=makeQuery(id+"F9.imprint","IMPRINT",FACE,{"disambiguationData":[TD([[makeQuery(id+"F9.imprint","IMPRINT",EDGE,{"disambiguationData":[TD([[subQ2,1.0]])],"derivedFrom":subQ1}),-1.0]])]});}
            var Q12;
            {var subQ0=sQuery(id+"F9.wireOp",EDGE,"E15.6");var subQ1=sQuery(id+"F9.wireOp",EDGE,"E15.5");var subQ2=makeQuery(id+"F9.imprint","INTERSECT",VERTEX,{"derivedFrom":[subQ1,subQ0]});Q12=makeQuery(id+"F9.imprint","IMPRINT",FACE,{"disambiguationData":[TD([[makeQuery(id+"F9.imprint","IMPRINT",EDGE,{"disambiguationData":[TD([[subQ2,1.0]])],"derivedFrom":subQ1}),-1.0]])]});}
            var Q13;
            {var subQ0=sQuery(id+"F9.wireOp",EDGE,"E15.6");var subQ1=sQuery(id+"F9.wireOp",EDGE,"E15.5");var subQ2=makeQuery(id+"F9.imprint","INTERSECT",VERTEX,{"derivedFrom":[subQ1,subQ0]});Q13=makeQuery(id+"F9.imprint","IMPRINT",FACE,{"disambiguationData":[TD([[makeQuery(id+"F9.imprint","IMPRINT",EDGE,{"disambiguationData":[TD([[subQ2,1.0]])],"derivedFrom":subQ1}),1.0]])]});}
            var Q14;
            {var subQ0=sQuery(id+"F9.wireOp",EDGE,"E15.5");var subQ1=sQuery(id+"F9.wireOp",EDGE,"E15.4");var subQ2=makeQuery(id+"F9.imprint","INTERSECT",VERTEX,{"derivedFrom":[subQ1,subQ0]});Q14=makeQuery(id+"F9.imprint","IMPRINT",FACE,{"disambiguationData":[TD([[makeQuery(id+"F9.imprint","IMPRINT",EDGE,{"disambiguationData":[TD([[subQ2,1.0]])],"derivedFrom":subQ1}),-1.0]])]});}
            var Q15;
            {var subQ0=sQuery(id+"F9.wireOp",EDGE,"E15.5");var subQ1=sQuery(id+"F9.wireOp",EDGE,"E15.4");var subQ2=makeQuery(id+"F9.imprint","INTERSECT",VERTEX,{"derivedFrom":[subQ1,subQ0]});Q15=makeQuery(id+"F9.imprint","IMPRINT",FACE,{"disambiguationData":[TD([[makeQuery(id+"F9.imprint","IMPRINT",EDGE,{"disambiguationData":[TD([[subQ2,1.0]])],"derivedFrom":subQ1}),1.0]])]});}
            extrude(context, id + "F10", {"entities" : qUnion([Q0, Q1, Q2, Q3, Q4, Q5, Q6, Q7, Q8, Q9, Q10, Q11, Q12, Q13, Q14, Q15]), "operationType" : NewBodyOperationType.REMOVE, "depth" : 4 * mm, "offsetDistance" : 25 * mm, "hasSecondDirection" : true, "secondDirectionOppositeDirection" : false, "secondDirectionDepth" : 3 * mm});
        }
        {
            var Q0;
            {var subQ0=sQuery(id+"F9.wireOp",EDGE,"E15.4");var subQ1=sQuery(id+"F9.wireOp",EDGE,"E15.3");var subQ2=makeQuery(id+"F9.imprint","INTERSECT",VERTEX,{"derivedFrom":[subQ1,subQ0]});Q0=makeQuery(id+"F9.imprint","IMPRINT",FACE,{"disambiguationData":[TD([[makeQuery(id+"F9.imprint","IMPRINT",EDGE,{"disambiguationData":[TD([[subQ2,1.0]])],"derivedFrom":subQ1}),1.0]])]});}
            var Q1;
            {var subQ0=sQuery(id+"F9.wireOp",EDGE,"E15.4");var subQ1=sQuery(id+"F9.wireOp",EDGE,"E15.3");var subQ2=makeQuery(id+"F9.imprint","INTERSECT",VERTEX,{"derivedFrom":[subQ1,subQ0]});Q1=makeQuery(id+"F9.imprint","IMPRINT",FACE,{"disambiguationData":[TD([[makeQuery(id+"F9.imprint","IMPRINT",EDGE,{"disambiguationData":[TD([[subQ2,1.0]])],"derivedFrom":subQ1}),-1.0]])]});}
            var Q2;
            {var subQ0=sQuery(id+"F9.wireOp",EDGE,"E15.7");var subQ1=sQuery(id+"F9.wireOp",EDGE,"E15.0");var subQ2=makeQuery(id+"F9.imprint","INTERSECT",VERTEX,{"derivedFrom":[subQ1,subQ0]});Q2=makeQuery(id+"F9.imprint","IMPRINT",FACE,{"disambiguationData":[TD([[makeQuery(id+"F9.imprint","IMPRINT",EDGE,{"disambiguationData":[TD([[subQ2,-1.0]])],"derivedFrom":subQ1}),1.0]])]});}
            var Q3;
            {var subQ0=sQuery(id+"F9.wireOp",EDGE,"E15.7");var subQ1=sQuery(id+"F9.wireOp",EDGE,"E15.0");var subQ2=makeQuery(id+"F9.imprint","INTERSECT",VERTEX,{"derivedFrom":[subQ1,subQ0]});Q3=makeQuery(id+"F9.imprint","IMPRINT",FACE,{"disambiguationData":[TD([[makeQuery(id+"F9.imprint","IMPRINT",EDGE,{"disambiguationData":[TD([[subQ2,-1.0]])],"derivedFrom":subQ1}),-1.0]])]});}
            extrude(context, id + "F11", {"entities" : qUnion([Q0, Q1, Q2, Q3]), "operationType" : NewBodyOperationType.ADD, "depth" : 22 * mm, "offsetDistance" : 25 * mm, "hasSecondDirection" : true, "secondDirectionOppositeDirection" : false, "secondDirectionDepth" : 21.4 * mm});
        }
        {
            var Q0;
            Q0=makeQuery(id+"F11.opExtrude","CAP_EDGE",EDGE,{"disambiguationData":[OSD([sQuery(id+"F9.wireOp",EDGE,"E20")])],"isStart":true});
            var Q1;
            Q1=makeQuery(id+"F11.opExtrude","CAP_EDGE",EDGE,{"disambiguationData":[OSD([sQuery(id+"F9.wireOp",EDGE,"E16")])],"isStart":true});
            fillet(context, id + "F12", {"entities" : qUnion([Q0, Q1]), "radius" : 0.5 * mm, "tangentPropagation" : true, "allowEdgeOverflow" : false});
        }
    });
